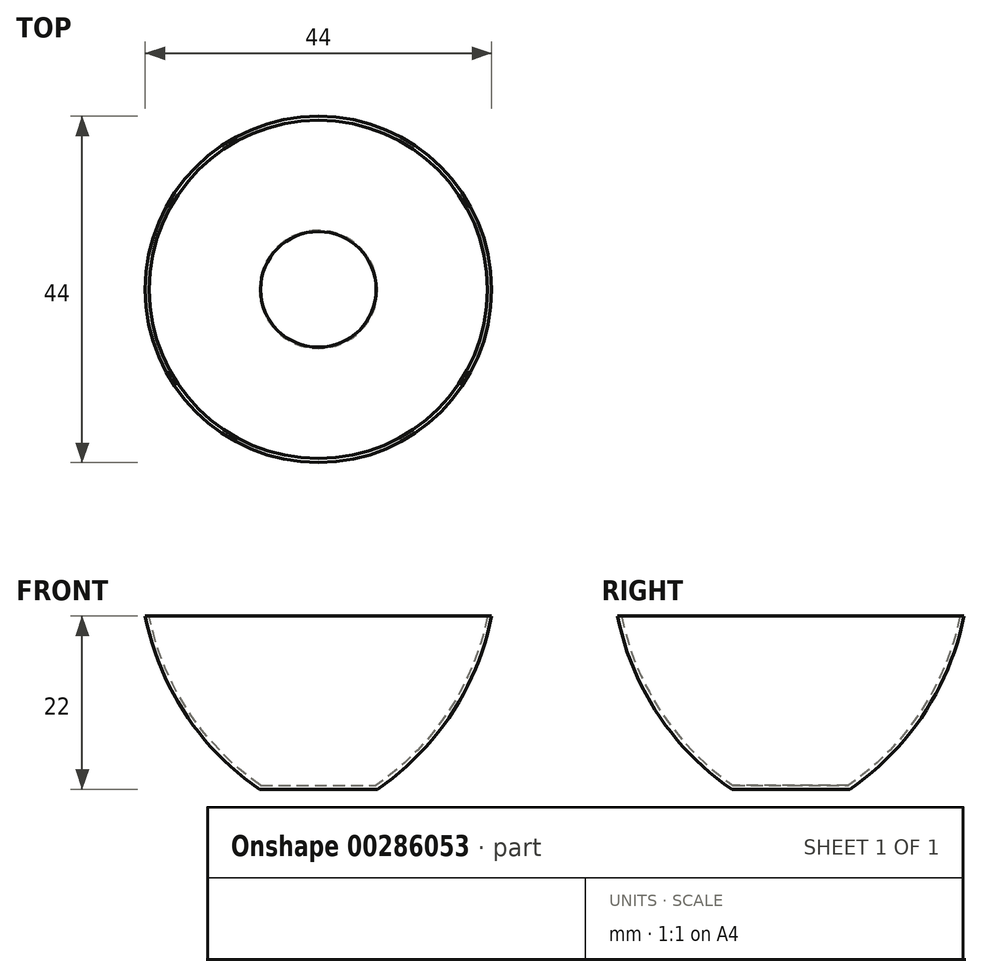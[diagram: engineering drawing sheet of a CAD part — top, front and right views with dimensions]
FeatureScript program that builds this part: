
annotation { "Feature Type Name" : "Feature", "Feature Type Description" : "" }
export const myFeature = defineFeature(function(context is Context, id is Id, definition is map)
    precondition{}
    {
        {
            var Q0;
            Q0=qCreatedBy(makeId("Front.planeOp"),FACE);
            var sketch = newSketch(context, id + "F0", { "sketchPlane" : qUnion([Q0])});
            skLineSegment(sketch, "E0", {"start": v(0, 0) * mm, "end": v(0, 36.82) * mm, "construction": true});
            skLineSegment(sketch, "E1", {"start": v(0, 0) * mm, "end": v(7.5, 0) * mm});
            skArc(sketch, "E2", {"start": v(7.5, 0) * mm, "mid": v(16.9, 9.58) * mm, "end": v(22, 22) * mm});
            skArc(sketch, "E3.0", {"start": v(7.34, 0.5) * mm, "mid": v(16.5, 9.88) * mm, "end": v(21.5, 22) * mm});
            skLineSegment(sketch, "E3.1", {"start": v(0, 0.5) * mm, "end": v(7.34, 0.5) * mm});
            skLineSegment(sketch, "E4", {"start": v(22, 22) * mm, "end": v(21.5, 22) * mm});
            skPoint(sketch, "E5.orphan", {"position": v(20.2, 22) * mm});
            skLineSegment(sketch, "E6", {"start": v(0, 0.5) * mm, "end": v(0, 0) * mm});
            skSolve(sketch);
        }
        {
            var Q0;
            Q0 = qSketchRegion(id + "F0", true);
            var Q1;
            Q1=sQuery(id+"F0.wireOp",EDGE,"E0");
            revolve(context, id + "F1", {"entities" : qUnion([Q0]), "axis" : qUnion([Q1]), "revolveType" : RevolveType.FULL});
        }
    });
